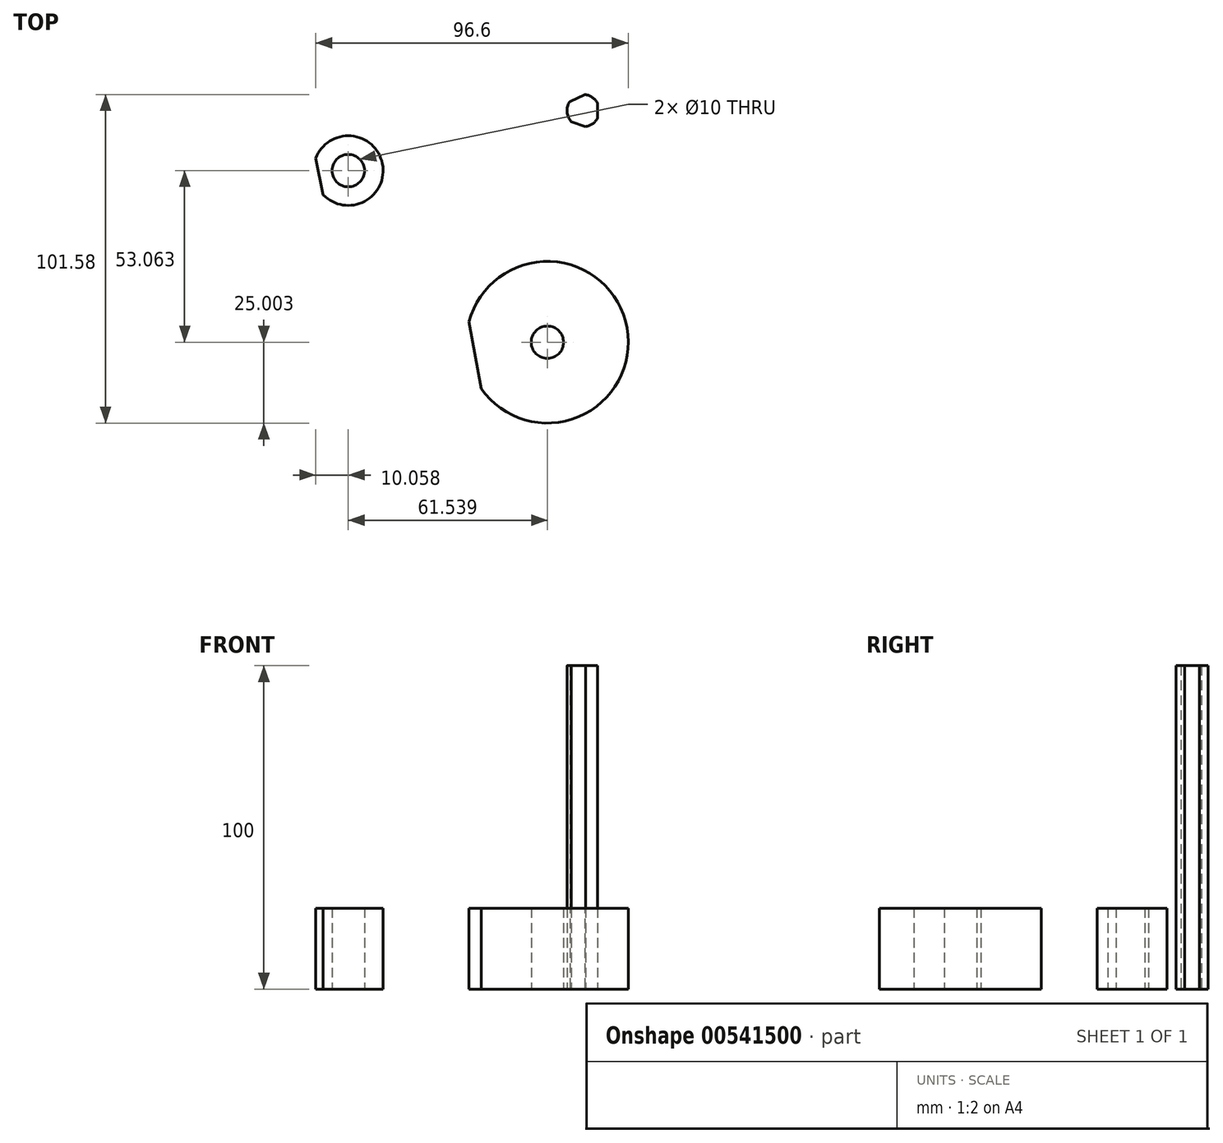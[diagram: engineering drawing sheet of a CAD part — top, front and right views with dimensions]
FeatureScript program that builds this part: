
annotation { "Feature Type Name" : "Feature", "Feature Type Description" : "" }
export const myFeature = defineFeature(function(context is Context, id is Id, definition is map)
    precondition{}
    {
        {
            var Q0;
            Q0=qCreatedBy(makeId("Top.planeOp"),FACE);
            var sketch = newSketch(context, id + "F0", { "sketchPlane" : qUnion([Q0])});
            skArc(sketch, "E0", {"start": v(-8, -36.63) * mm, "mid": v(37.07, -17.83) * mm, "end": v(-11.73, -16) * mm});
            skArc(sketch, "E1", {"start": v(-56.8, 23.28) * mm, "mid": v(-38.52, 32.95) * mm, "end": v(-59.13, 34.64) * mm});
            skCircle(sketch, "E2", {"center": v(-49.07, 30.79) * mm, "radius": 5 * mm});
            skCircle(sketch, "E3", {"center": v(12.47, -22.28) * mm, "radius": 5 * mm});
            skArc(sketch, "E4", {"start": v(19.42, 52.18) * mm, "mid": v(18.54, 48.98) * mm, "end": v(19.86, 45.93) * mm});
            skLineSegment(sketch, "E5", {"start": v(-11.73, -16) * mm, "end": v(-8, -36.63) * mm});
            skLineSegment(sketch, "E6", {"start": v(-59.13, 34.64) * mm, "end": v(-56.8, 23.28) * mm});
            skLineSegment(sketch, "E7", {"start": v(19.86, 45.93) * mm, "end": v(24.25, 44.38) * mm});
            skLineSegment(sketch, "E8", {"start": v(19.42, 52.18) * mm, "end": v(24.09, 54.3) * mm});
            skLineSegment(sketch, "E9", {"start": v(27.98, 47.06) * mm, "end": v(27.98, 51.6) * mm});
            skArc(sketch, "E10.trimOffspring", {"start": v(24.25, 44.38) * mm, "mid": v(26.44, 45.27) * mm, "end": v(27.98, 47.06) * mm});
            skArc(sketch, "E11.trimOffspring", {"start": v(27.98, 51.6) * mm, "mid": v(26.37, 53.44) * mm, "end": v(24.09, 54.3) * mm});
            skSolve(sketch);
        }
        {
            var Q0;
            Q0=makeQuery(id+"F0.imprint","IMPRINT",FACE,{"disambiguationData":[TD([[makeQuery(id+"F0.imprint","IMPRINT",EDGE,{"derivedFrom":sQuery(id+"F0.wireOp",EDGE,"E1")}),1.0]])]});
            extrude(context, id + "F1", {"entities" : qUnion([Q0]), "depth" : 25 * mm, "offsetDistance" : 25 * mm});
        }
        {
            var Q0;
            Q0=makeQuery(id+"F0.imprint","IMPRINT",FACE,{"disambiguationData":[TD([[makeQuery(id+"F0.imprint","IMPRINT",EDGE,{"derivedFrom":sQuery(id+"F0.wireOp",EDGE,"E0")}),1.0]])]});
            extrude(context, id + "F2", {"entities" : qUnion([Q0]), "depth" : 25 * mm, "offsetDistance" : 25 * mm});
        }
        {
            var Q0;
            Q0=makeQuery(id+"F0.imprint","IMPRINT",FACE,{"disambiguationData":[TD([[makeQuery(id+"F0.imprint","IMPRINT",EDGE,{"derivedFrom":sQuery(id+"F0.wireOp",EDGE,"E4")}),1.0]])]});
            extrude(context, id + "F3", {"entities" : qUnion([Q0]), "depth" : 100 * mm, "offsetDistance" : 25 * mm});
        }
    });
